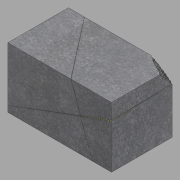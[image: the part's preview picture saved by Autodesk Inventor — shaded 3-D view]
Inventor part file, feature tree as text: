
AUTODESK INVENTOR PART (.ipt)
format: ipt  version: 2022.1 (Build 261234020, 234B)  size: 1,104,896 bytes
history: native  units: in
note: dims shown in document units (in); Inventor stores cm internally (conversion verified against a paired STEP export)
features: other x3, sketch x2, loft x1
ambient origin geometry x8: Origin, YZ Plane, XZ Plane, XY Plane, X Axis, Y Axis, Z Axis, Center Point
bodies: Solid1 (feature_tree)
feature tree (6):
  other  "4th.ipt"
  loft  "Loft1"
  other  "Solid1::4th.ipt"
  other  "TaggingFeature1"
  sketch  "Sketch1"  dims[d0=0.3937in d1=0.0in d2=90.0deg]
  sketch  "Sketch2"  dims[d3=0.0in d4=90.0deg]
